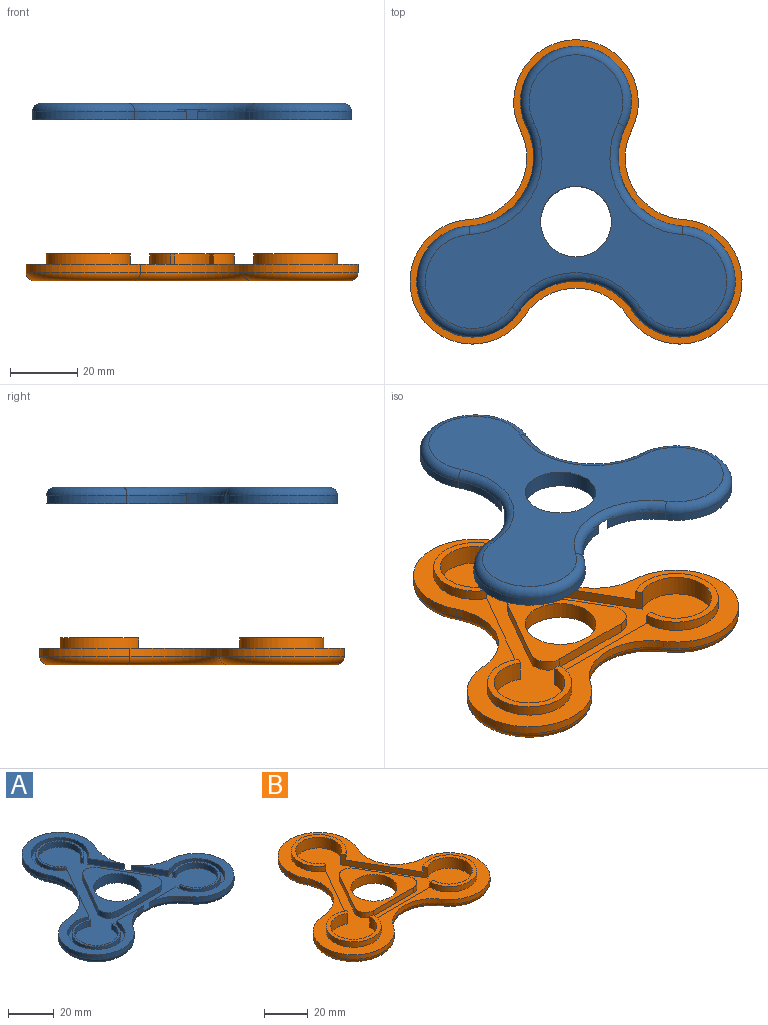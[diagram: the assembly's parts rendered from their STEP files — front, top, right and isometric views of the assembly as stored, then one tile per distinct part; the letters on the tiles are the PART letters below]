
ASSEMBLY  parts=2 mates=1
PART A: 52 faces, bbox 97.3x89.1x5 mm
  f0: cylinder r=20.4mm len=17.77mm, axis (0,0,-1), area 45.2mm2, adj f3,f6,f17,f43
  f1: cylinder r=20.4mm len=15.27mm, axis (0,0,-1), area 45.2mm2, adj f4,f8,f20,f42
  f2: cylinder r=20.4mm len=15.5mm, axis (0,0,-1), area 45.2mm2, adj f10,f13,f16,f48
  f3: plane 41.65x33mm, normal (0,0,1), area 360mm2, adj f0,f6,f12,f22,f43,f47
  f4: plane 45.54x41.65mm, normal (0,0,1), area 360mm2, adj f1,f7,f8,f23,f42,f44
  f5: plane 35.62x31.84mm, normal (0,0,1), area 395.4mm2, adj f11,f41,f45,f46,f49,f50,f51
  f6: cylinder r=16.5mm len=33mm, axis (0,0,-1), area 165.2mm2, adj f0,f3,f12,f15
  f7: cylinder r=20.4mm len=15.5mm, axis (0,0,-1), area 45.2mm2, adj f4,f8,f17,f44
  f8: cylinder r=16.5mm len=32.97mm, axis (0,0,-1), area 165.2mm2, adj f1,f4,f7,f19
  f9: cylinder r=20.4mm len=15.27mm, axis (0,0,-1), area 45.2mm2, adj f10,f13,f20,f40
  f10: cylinder r=16.5mm len=32.97mm, axis (0,0,-1), area 165.2mm2, adj f2,f9,f13,f18
  f11: cylinder r=10.5mm len=21mm, axis (0,0,-1), area 329.9mm2, adj f5,f14
  f12: cylinder r=20.4mm len=17.77mm, axis (0,0,-1), area 45.2mm2, adj f3,f6,f16,f47
  f13: plane 45.54x41.65mm, normal (0,0,1), area 360mm2, adj f2,f9,f10,f21,f40,f48
  f14: plane 89.51x81.26mm, normal (0,0,-1), area 2804.7mm2, adj f11,f15,f16,f17,f18,f19,f20
  f15: torus R=13.96mm, axis (0,0,1), area 252.9mm2, adj f6,f14,f16,f17
  f16: torus R=22.94mm, axis (0,0,1), area 165.9mm2, adj f2,f12,f14,f15,f18,f24,f47,f48
  f17: torus R=22.94mm, axis (0,0,1), area 165.9mm2, adj f0,f7,f14,f15,f19,f24,f43,f44
  f18: torus R=13.96mm, axis (0,0,1), area 252.9mm2, adj f10,f14,f16,f20
  f19: torus R=13.96mm, axis (0,0,1), area 252.9mm2, adj f8,f14,f17,f20
  f20: torus R=22.94mm, axis (0,0,1), area 165.9mm2, adj f1,f9,f14,f18,f19,f24,f40,f42
  f21: cylinder r=12.5mm len=25mm, axis (0,0,1), area 196.3mm2, adj f13,f24,f40,f48
  f22: cylinder r=12.5mm len=25mm, axis (0,0,1), area 196.3mm2, adj f3,f24,f43,f47
  f23: cylinder r=12.5mm len=25mm, axis (0,0,1), area 196.3mm2, adj f4,f24,f42,f44
  f24: plane 86.59x78.34mm, normal (0,0,1), area 1969.7mm2, adj f16,f17,f20,f21,f22,f23,f26,f27
  f25: plane 21x19.59mm, normal (0,0,1), area 52.4mm2, adj f26,f27,f38,f39
  f26: cylinder r=10.5mm len=21mm, axis (0,0,1), area 164.9mm2, adj f24,f25,f38,f39
  f27: cylinder r=9.5mm len=19mm, axis (0,0,1), area 149.2mm2, adj f24,f25,f38,f39
  f28: plane 21x21mm, normal (0,0,1), area 52.4mm2, adj f29,f30,f36,f37
  f29: cylinder r=10.5mm len=21mm, axis (0,0,1), area 164.9mm2, adj f24,f28,f36,f37
  f30: cylinder r=9.5mm len=19mm, axis (0,0,1), area 149.2mm2, adj f24,f28,f36,f37
  f31: plane 21x21mm, normal (0,0,1), area 52.4mm2, adj f32,f33,f34,f35
  f32: cylinder r=10.5mm len=21mm, axis (0,0,1), area 164.9mm2, adj f24,f31,f34,f35
  f33: cylinder r=9.5mm len=19mm, axis (0,0,1), area 149.2mm2, adj f24,f31,f34,f35
  f34: plane 3x1mm, normal (0,1,0), area 3mm2, adj f24,f31,f32,f33
  f35: plane 3x0.87mm, normal (-0.87,-0.5,0), area 3mm2, adj f24,f31,f32,f33
  f36: plane 3x0.87mm, normal (0.87,-0.5,0), area 3mm2, adj f24,f28,f29,f30
  f37: plane 3x1mm, normal (0,1,0), area 3mm2, adj f24,f28,f29,f30
  f38: plane 3x0.87mm, normal (-0.87,-0.5,0), area 3mm2, adj f24,f25,f26,f27
  f39: plane 3x0.87mm, normal (0.87,-0.5,0), area 3mm2, adj f24,f25,f26,f27
  f40: plane 16.54x3mm, normal (0,1,0), area 49.5mm2, adj f9,f13,f20,f21,f24
  f41: plane 25.46x3mm, normal (0,-1,0), area 76.4mm2, adj f5,f24,f50,f51
  f42: plane 16.54x3mm, normal (0,1,0), area 49.5mm2, adj f1,f4,f20,f23,f24
  f43: plane 14.33x8.27mm, normal (0.87,-0.5,0), area 49.5mm2, adj f0,f3,f17,f22,f24
  f44: plane 14.33x8.27mm, normal (0.87,-0.5,0), area 49.5mm2, adj f4,f7,f17,f23,f24
  f45: plane 21.68x12.73mm, normal (-0.86,0.51,0), area 75.4mm2, adj f5,f24,f49,f50
  f46: plane 21.68x12.73mm, normal (0.86,0.51,0), area 75.4mm2, adj f5,f24,f49,f51
  f47: plane 14.33x8.27mm, normal (-0.87,-0.5,0), area 49.5mm2, adj f3,f12,f16,f22,f24
  f48: plane 14.33x8.27mm, normal (-0.87,-0.5,0), area 49.5mm2, adj f2,f13,f16,f21,f24
  f49: cylinder r=5.08mm len=8.76mm, axis (0,0,-1), area 31.7mm2, adj f5,f24,f45,f46
  f50: cylinder r=5.08mm len=7.65mm, axis (0,0,1), area 32mm2, adj f5,f24,f41,f45
  f51: cylinder r=5.08mm len=7.65mm, axis (0,0,1), area 32mm2, adj f5,f24,f41,f46
PART B: 35 faces, bbox 101.6x93.4x8 mm
  f0: plane 98.59x90.34mm, normal (0,0,1), area 1736.7mm2, adj f3,f6,f9,f11,f12,f13,f14,f15
  f1: plane 35.97x32.51mm, normal (0,0,1), area 416.4mm2, adj f16,f28,f29,f30,f32,f33,f34
  f2: plane 25x23.33mm, normal (0,0,1), area 120.4mm2, adj f3,f4,f26,f27
  f3: cylinder r=12.5mm len=25mm, axis (0,0,1), area 196.3mm2, adj f0,f2,f26,f27
  f4: cylinder r=10.5mm len=21mm, axis (0,0,-1), area 329.9mm2, adj f2,f25,f26,f27
  f5: plane 25x25mm, normal (0,0,1), area 120.4mm2, adj f6,f7,f27,f31
  f6: cylinder r=12.5mm len=25mm, axis (0,0,1), area 196.3mm2, adj f0,f5,f27,f31
  f7: cylinder r=10.5mm len=21mm, axis (0,0,-1), area 329.9mm2, adj f5,f25,f27,f31
  f8: plane 25x25mm, normal (0,0,1), area 120.4mm2, adj f9,f10,f26,f31
  f9: cylinder r=12.5mm len=25mm, axis (0,0,1), area 196.3mm2, adj f0,f8,f26,f31
  f10: cylinder r=10.5mm len=21mm, axis (0,0,-1), area 329.9mm2, adj f8,f25,f26,f31
  f11: cylinder r=18.5mm len=37mm, axis (0,0,-1), area 185.2mm2, adj f0,f12,f17,f24
  f12: cylinder r=18.4mm len=26.59mm, axis (0,0,-1), area 89.4mm2, adj f0,f11,f13,f23
  f13: cylinder r=18.5mm len=36.97mm, axis (0,0,-1), area 185.2mm2, adj f0,f12,f14,f21
  f14: cylinder r=18.4mm len=30.71mm, axis (0,0,-1), area 89.4mm2, adj f0,f13,f15,f19
  f15: cylinder r=18.5mm len=36.97mm, axis (0,0,-1), area 185.2mm2, adj f0,f14,f17,f20
  f16: cylinder r=10.5mm len=21mm, axis (0,0,-1), area 329.9mm2, adj f1,f18
  f17: cylinder r=18.4mm len=26.59mm, axis (0,0,-1), area 89.4mm2, adj f0,f11,f15,f22
  f18: plane 93.51x85.26mm, normal (0,0,-1), area 3430mm2, adj f16,f19,f20,f21,f22,f23,f24
  f19: torus R=20.94mm, axis (0,0,1), area 152.2mm2, adj f14,f18,f20,f21
  f20: torus R=15.96mm, axis (0,0,1), area 285.4mm2, adj f15,f18,f19,f22
  f21: torus R=15.96mm, axis (0,0,1), area 285.4mm2, adj f13,f18,f19,f23
  f22: torus R=20.94mm, axis (0,0,1), area 152.2mm2, adj f17,f18,f20,f24
  f23: torus R=20.94mm, axis (0,0,1), area 152.2mm2, adj f12,f18,f21,f24
  f24: torus R=15.96mm, axis (0,0,1), area 285.4mm2, adj f11,f18,f22,f23
  f25: plane 82.59x74.34mm, normal (0,0,1), area 1745.8mm2, adj f4,f7,f10,f26,f27,f28,f29,f30
  f26: plane 35.15x20.3mm, normal (-0.87,-0.5,0), area 133.8mm2, adj f0,f2,f3,f4,f8,f9,f10,f25
  f27: plane 35.15x20.3mm, normal (0.87,-0.5,0), area 133.8mm2, adj f0,f2,f3,f4,f5,f6,f7,f25
  f28: plane 22.35x12.9mm, normal (-0.87,0.5,0), area 77.4mm2, adj f1,f25,f32,f33
  f29: plane 22.35x12.9mm, normal (0.87,0.5,0), area 77.4mm2, adj f1,f25,f32,f34
  f30: plane 25.81x3mm, normal (0,-1,0), area 77.4mm2, adj f1,f25,f33,f34
  f31: plane 40.59x6mm, normal (0,1,0), area 133.8mm2, adj f0,f5,f6,f7,f8,f9,f10,f25
  f32: cylinder r=5.08mm len=8.8mm, axis (0,0,-1), area 31.9mm2, adj f1,f25,f28,f29
  f33: cylinder r=5.08mm len=7.62mm, axis (0,0,-1), area 31.9mm2, adj f1,f25,f28,f30
  f34: cylinder r=5.08mm len=7.62mm, axis (0,0,-1), area 31.9mm2, adj f1,f25,f29,f30
PLACE A rot(axis=(0,1,0),180deg) t=(-27.66,-19.97,55.88)mm
PLACE B t=(-27.66,-19.97,3.08)mm fixed
MATE slider A.f22 <-> B.f3  axis (0,0,-1) through (-27.66,15.59,50.88)mm
